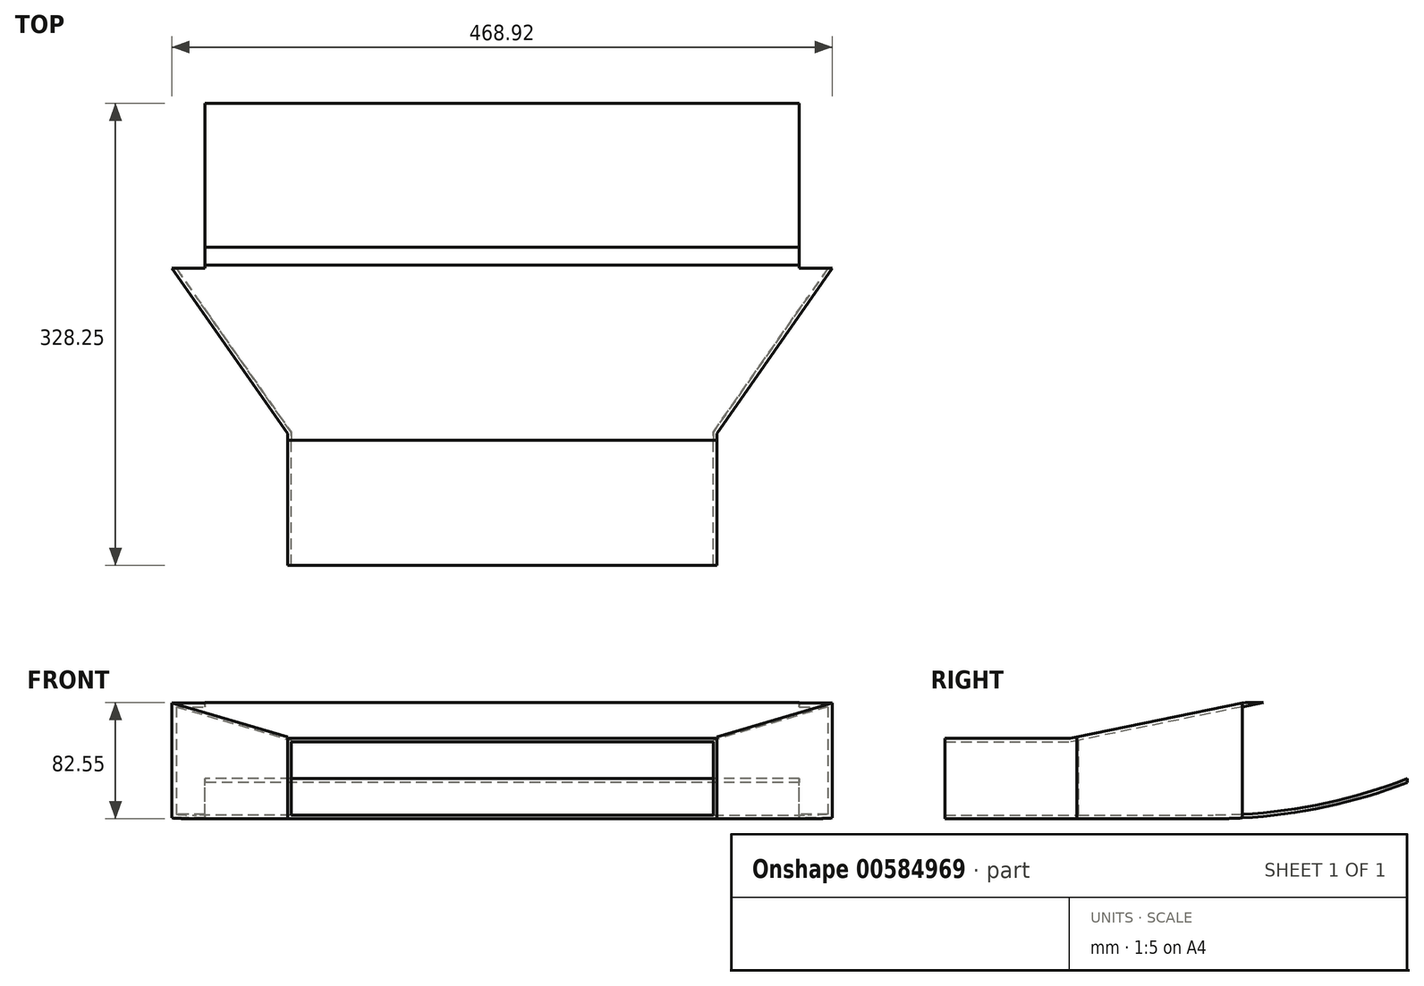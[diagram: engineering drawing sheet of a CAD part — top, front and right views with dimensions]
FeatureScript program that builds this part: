
annotation { "Feature Type Name" : "Feature", "Feature Type Description" : "" }
export const myFeature = defineFeature(function(context is Context, id is Id, definition is map)
    precondition{}
    {
        {
            var Q0;
            Q0=qCreatedBy(makeId("Top.planeOp"),FACE);
            var sketch = newSketch(context, id + "F0", { "sketchPlane" : qUnion([Q0])});
            skPoint(sketch, "E0.middle", {"position": v(0, 0) * mm});
            skLineSegment(sketch, "E1.bottom", {"start": v(234.46, 58.62) * mm, "end": v(211.02, 58.62) * mm});
            skPoint(sketch, "E1.middle", {"position": v(0, 9.95) * mm});
            skLineSegment(sketch, "E2.bottom", {"start": v(211.02, 175.85) * mm, "end": v(-211.02, 175.85) * mm});
            skLineSegment(sketch, "E2.left", {"start": v(211.02, 175.85) * mm, "end": v(211.02, 58.62) * mm});
            skLineSegment(sketch, "E2.right", {"start": v(-211.02, 175.85) * mm, "end": v(-211.02, 58.62) * mm});
            skPoint(sketch, "E2.middle", {"position": v(0, 117.23) * mm});
            skLineSegment(sketch, "E3", {"start": v(-152.4, -58.62) * mm, "end": v(-234.46, 58.62) * mm});
            skLineSegment(sketch, "E4", {"start": v(152.4, -58.62) * mm, "end": v(234.46, 58.62) * mm});
            skLineSegment(sketch, "E5.bottom", {"start": v(152.4, -152.4) * mm, "end": v(-152.4, -152.4) * mm});
            skLineSegment(sketch, "E5.left", {"start": v(152.4, -152.4) * mm, "end": v(152.4, -58.62) * mm});
            skLineSegment(sketch, "E5.right", {"start": v(-152.4, -152.4) * mm, "end": v(-152.4, -58.62) * mm});
            skPoint(sketch, "E5.middle", {"position": v(0, -80.45) * mm});
            skPoint(sketch, "E5.middle.positionSnap0", {"position": v(0, -38.71) * mm});
            skPoint(sketch, "E5.centerSnap0", {"position": v(0, -38.71) * mm});
            skPoint(sketch, "E6.orphan", {"position": v(-152.4, -8.5) * mm});
            skLineSegment(sketch, "E7.trimOffspring", {"start": v(-211.02, 58.62) * mm, "end": v(-234.46, 58.62) * mm});
            skPoint(sketch, "E0.bottom.end.orphan", {"position": v(-152.4, 58.62) * mm});
            skPoint(sketch, "E8.orphan", {"position": v(152.4, 58.62) * mm});
            skPoint(sketch, "E1.right.end.orphan", {"position": v(-234.46, -38.71) * mm});
            skPoint(sketch, "E1.left.end.orphan", {"position": v(234.46, -38.71) * mm});
            skPoint(sketch, "E9.orphan", {"position": v(152.4, -8.5) * mm});
            skLineSegment(sketch, "E10", {"start": v(-339.9, 68.69) * mm, "end": v(-297.79, 147.3) * mm});
            skSolve(sketch);
        }
        {
            var Q0;
            Q0=makeQuery(id+"F0.imprint","IMPRINT",FACE,{"disambiguationData":[TD([[makeQuery(id+"F0.imprint","IMPRINT",EDGE,{"derivedFrom":sQuery(id+"F0.wireOp",EDGE,"E1.bottom")}),1.0]])]});
            extrude(context, id + "F1", {"entities" : qUnion([Q0]), "depth" : 82.55 * mm, "offsetDistance" : 25.4 * mm});
        }
        {
            var Q0;
            Q0=qCreatedBy(makeId("Right.planeOp"),FACE);
            var sketch = newSketch(context, id + "F2", { "sketchPlane" : qUnion([Q0])});
            skLineSegment(sketch, "E11.bottom", {"start": v(-165.1, 0) * mm, "end": v(-63.5, 0) * mm});
            skLineSegment(sketch, "E11.top", {"start": v(-165.1, 57.15) * mm, "end": v(-63.5, 57.15) * mm});
            skLineSegment(sketch, "E11.left", {"start": v(-165.1, 0) * mm, "end": v(-165.1, 57.15) * mm});
            skLineSegment(sketch, "E12.top", {"start": v(60.93, 82.55) * mm, "end": v(190.47, 82.55) * mm});
            skLineSegment(sketch, "E13", {"start": v(60.93, 82.55) * mm, "end": v(-63.5, 57.15) * mm});
            skLineSegment(sketch, "E14", {"start": v(38.1, 0) * mm, "end": v(-63.5, 0) * mm});
            skLineSegment(sketch, "E15", {"start": v(190.47, 82.55) * mm, "end": v(190.47, 31.75) * mm});
            skArc(sketch, "E16", {"start": v(38.1, 0) * mm, "mid": v(115.92, 8.02) * mm, "end": v(190.47, 31.75) * mm});
            skSolve(sketch);
        }
        {
            var Q0;
            Q0=makeQuery(id+"F2.imprint","IMPRINT",FACE,{"disambiguationData":[TD([[makeQuery(id+"F2.imprint","IMPRINT",EDGE,{"derivedFrom":sQuery(id+"F2.wireOp",EDGE,"E11.bottom")}),1.0]])]});
            extrude(context, id + "F3", {"entities" : qUnion([Q0]), "operationType" : NewBodyOperationType.INTERSECT, "endBound" : BoundingType.SYMMETRIC, "depth" : 508 * mm, "offsetDistance" : 25.4 * mm});
        }
        {
            var Q0;
            Q0=makeQuery(id+"F3.boolean.opBoolean","COPY",FACE,{"derivedFrom":makeQuery(id+"F3.boolean.toolComplement.opBoolean","COPY",FACE,{"derivedFrom":makeQuery(id+"F3.opExtrude","SWEPT_FACE",FACE,{"disambiguationData":[OSD([sQuery(id+"F2.wireOp",EDGE,"E11.top")])]})})});
            var Q1;
            Q1=makeQuery(id+"F1.opExtrude","SWEPT_FACE",FACE,{"disambiguationData":[OSD([sQuery(id+"F0.wireOp",EDGE,"E5.bottom")])]});
            var Q2;
            Q2=makeQuery(id+"F1.opExtrude","SWEPT_FACE",FACE,{"disambiguationData":[OSD([sQuery(id+"F0.wireOp",EDGE,"E2.bottom")])]});
            var Q3;
            Q3=makeQuery(id+"F1.opExtrude","SWEPT_FACE",FACE,{"disambiguationData":[OSD([sQuery(id+"F0.wireOp",EDGE,"E2.right")])]});
            var Q4;
            Q4=makeQuery(id+"F1.opExtrude","SWEPT_FACE",FACE,{"disambiguationData":[OSD([sQuery(id+"F0.wireOp",EDGE,"E2.left")])]});
            var Q5;
            Q5=makeQuery(id+"F1.opExtrude","SWEPT_FACE",FACE,{"disambiguationData":[OSD([sQuery(id+"F0.wireOp",EDGE,"E1.bottom")])]});
            var Q6;
            Q6=makeQuery(id+"F1.opExtrude","SWEPT_FACE",FACE,{"disambiguationData":[OSD([sQuery(id+"F0.wireOp",EDGE,"E7.trimOffspring")])]});
            var Q7;
            Q7=makeQuery(id+"F1.opExtrude","CAP_FACE",FACE,{"disambiguationData":[OSD([sQuery(id+"F0.wireOp",EDGE,"E1.bottom"),sQuery(id+"F0.wireOp",EDGE,"E2.bottom"),sQuery(id+"F0.wireOp",EDGE,"E2.left"),sQuery(id+"F0.wireOp",EDGE,"E2.right"),sQuery(id+"F0.wireOp",EDGE,"E3"),sQuery(id+"F0.wireOp",EDGE,"E4"),sQuery(id+"F0.wireOp",EDGE,"E5.bottom"),sQuery(id+"F0.wireOp",EDGE,"E5.left"),sQuery(id+"F0.wireOp",EDGE,"E5.right"),sQuery(id+"F0.wireOp",EDGE,"E7.trimOffspring")])],"isStart":false});
            var Q8;
            Q8=makeQuery(id+"F3.boolean.opBoolean","COPY",FACE,{"derivedFrom":makeQuery(id+"F3.boolean.toolComplement.opBoolean","COPY",FACE,{"derivedFrom":makeQuery(id+"F3.opExtrude","SWEPT_FACE",FACE,{"disambiguationData":[OSD([sQuery(id+"F2.wireOp",EDGE,"E12.right")])]})})});
            var Q9;
            Q9=makeQuery(id+"F3.boolean.opBoolean","COPY",FACE,{"derivedFrom":makeQuery(id+"F3.boolean.toolComplement.opBoolean","COPY",FACE,{"derivedFrom":makeQuery(id+"F3.opExtrude","SWEPT_FACE",FACE,{"disambiguationData":[OSD([sQuery(id+"F2.wireOp",EDGE,"E13")])]})})});
            var Q10;
            Q10=makeQuery(id+"F3.boolean.opBoolean","COPY",FACE,{"derivedFrom":makeQuery(id+"F3.boolean.toolComplement.opBoolean","COPY",FACE,{"derivedFrom":makeQuery(id+"F3.opExtrude","SWEPT_FACE",FACE,{"disambiguationData":[OSD([sQuery(id+"F2.wireOp",EDGE,"E15")])]})})});
            shell(context, id + "F4", {"entities" : qUnion([Q0, Q1, Q2, Q3, Q4, Q5, Q6, Q7, Q8, Q9, Q10]), "thickness" : 2.54 * mm});
        }
    });
